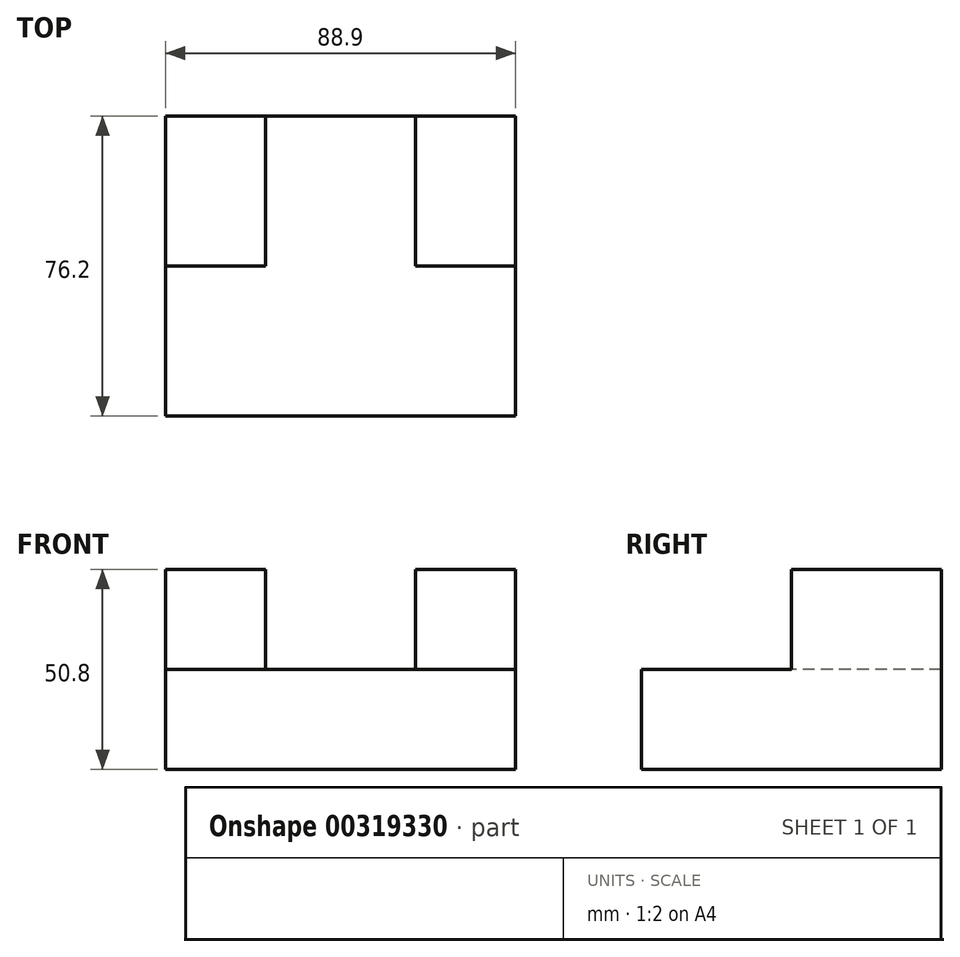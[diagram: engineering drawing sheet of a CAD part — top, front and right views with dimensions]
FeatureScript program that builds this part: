
annotation { "Feature Type Name" : "Feature", "Feature Type Description" : "" }
export const myFeature = defineFeature(function(context is Context, id is Id, definition is map)
    precondition{}
    {
        {
            var Q0;
            Q0=qCreatedBy(makeId("Top.planeOp"),FACE);
            var sketch = newSketch(context, id + "F0", { "sketchPlane" : qUnion([Q0])});
            skLineSegment(sketch, "E0.bottom", {"start": v(-42.39, 47.94) * mm, "end": v(46.51, 47.94) * mm});
            skLineSegment(sketch, "E0.top", {"start": v(-42.39, -28.26) * mm, "end": v(46.51, -28.26) * mm});
            skLineSegment(sketch, "E0.left", {"start": v(-42.39, 47.94) * mm, "end": v(-42.39, -28.26) * mm});
            skLineSegment(sketch, "E0.right", {"start": v(46.51, 47.94) * mm, "end": v(46.51, -28.26) * mm});
            skSolve(sketch);
        }
        {
            var Q0;
            Q0 = qSketchRegion(id + "F0", true);
            extrude(context, id + "F1", {"entities" : qUnion([Q0]), "depth" : 25.4 * mm});
        }
        {
            var Q0;
            Q0=makeQuery(id+"F1.opExtrude","CAP_FACE",FACE,{"disambiguationData":[OSD([sQuery(id+"F0.wireOp",EDGE,"E0.bottom"),sQuery(id+"F0.wireOp",EDGE,"E0.top"),sQuery(id+"F0.wireOp",EDGE,"E0.left"),sQuery(id+"F0.wireOp",EDGE,"E0.right")])],"isStart":false});
            var sketch = newSketch(context, id + "F2", { "sketchPlane" : qUnion([Q0])});
            skLineSegment(sketch, "E1", {"start": v(-42.39, 47.94) * mm, "end": v(-42.39, 9.84) * mm});
            skLineSegment(sketch, "E2", {"start": v(-42.39, 9.84) * mm, "end": v(-16.99, 9.84) * mm});
            skLineSegment(sketch, "E3", {"start": v(-16.99, 9.84) * mm, "end": v(-16.99, 47.94) * mm});
            skLineSegment(sketch, "E4", {"start": v(-16.99, 47.94) * mm, "end": v(-42.39, 47.94) * mm});
            skSolve(sketch);
        }
        {
            var Q0;
            Q0 = qSketchRegion(id + "F2", true);
            extrude(context, id + "F3", {"entities" : qUnion([Q0]), "operationType" : NewBodyOperationType.ADD, "depth" : 25.4 * mm});
        }
        {
            var Q0;
            Q0=makeQuery(id+"F1.opExtrude","CAP_FACE",FACE,{"disambiguationData":[OSD([sQuery(id+"F0.wireOp",EDGE,"E0.bottom"),sQuery(id+"F0.wireOp",EDGE,"E0.top"),sQuery(id+"F0.wireOp",EDGE,"E0.left"),sQuery(id+"F0.wireOp",EDGE,"E0.right")])],"isStart":false});
            var sketch = newSketch(context, id + "F4", { "sketchPlane" : qUnion([Q0])});
            skLineSegment(sketch, "E5", {"start": v(21.11, 47.94) * mm, "end": v(21.11, 9.84) * mm});
            skLineSegment(sketch, "E6", {"start": v(21.11, 9.84) * mm, "end": v(46.51, 9.84) * mm});
            skLineSegment(sketch, "E7", {"start": v(46.51, 9.84) * mm, "end": v(46.51, 47.94) * mm});
            skLineSegment(sketch, "E8", {"start": v(46.51, 47.94) * mm, "end": v(21.11, 47.94) * mm});
            skSolve(sketch);
        }
        {
            var Q0;
            Q0 = qSketchRegion(id + "F4", true);
            extrude(context, id + "F5", {"entities" : qUnion([Q0]), "operationType" : NewBodyOperationType.ADD, "depth" : 25.4 * mm});
        }
    });
